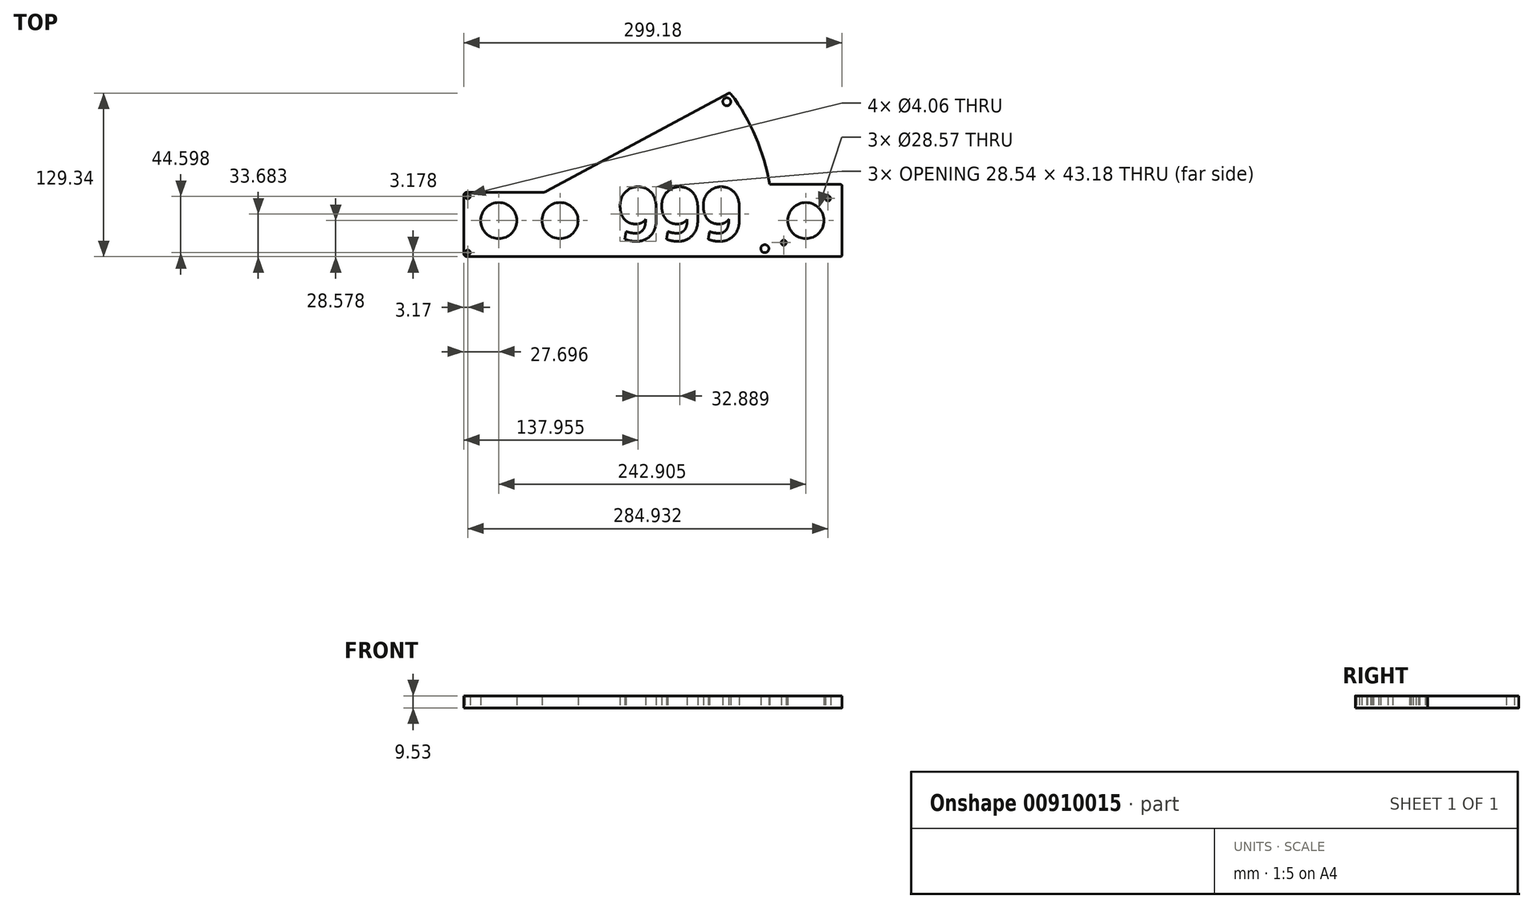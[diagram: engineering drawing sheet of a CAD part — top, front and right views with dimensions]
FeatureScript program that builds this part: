
annotation { "Feature Type Name" : "Feature", "Feature Type Description" : "" }
export const myFeature = defineFeature(function(context is Context, id is Id, definition is map)
    precondition{}
    {
        {
            var Q0;
            Q0=qCreatedBy(makeId("Top.planeOp"),FACE);
            var sketch = newSketch(context, id + "F0", { "sketchPlane" : qUnion([Q0])});
            skCircle(sketch, "E0", {"center": v(-130.35, 17.45) * mm, "radius": 14.29 * mm});
            skCircle(sketch, "E1", {"center": v(-130.35, 17.45) * mm, "radius": 25.4 * mm});
            skLineSegment(sketch, "E2", {"start": v(-130.35, -11.13) * mm, "end": v(36.65, -11.13) * mm});
            skArc(sketch, "E3", {"start": v(35.48, 46.02) * mm, "mid": v(24.35, 83.66) * mm, "end": v(4.8, 117.7) * mm});
            skLineSegment(sketch, "E4", {"start": v(3.18, 118.06) * mm, "end": v(-140.97, 40.58) * mm});
            skPoint(sketch, "E5.visualSharp", {"position": v(37.92, -11.13) * mm});
            skArc(sketch, "E5.filletArc", {"start": v(36.65, -11.13) * mm, "mid": v(37.55, -10.76) * mm, "end": v(37.92, -9.86) * mm});
            skPoint(sketch, "E6.visualSharp", {"position": v(4.14, 118.57) * mm});
            skArc(sketch, "E6.filletArc", {"start": v(4.8, 117.7) * mm, "mid": v(4.06, 118.18) * mm, "end": v(3.18, 118.06) * mm});
            skCircle(sketch, "E7", {"center": v(1.53, 111.4) * mm, "radius": 3.17 * mm});
            skCircle(sketch, "E8", {"center": v(31.57, -4.78) * mm, "radius": 3.17 * mm});
            skArc(sketch, "E9", {"start": v(25.22, 17.45) * mm, "mid": v(16.9, 67.65) * mm, "end": v(-7.18, 112.49) * mm});
            skLineSegment(sketch, "E10", {"start": v(-155.75, -11.13) * mm, "end": v(-130.35, -11.13) * mm});
            skLineSegment(sketch, "E11", {"start": v(25.22, 17.45) * mm, "end": v(25.22, -11.13) * mm});
            skLineSegment(sketch, "E12", {"start": v(-155.75, -11.13) * mm, "end": v(-204.01, -11.13) * mm});
            skLineSegment(sketch, "E13", {"start": v(-206.55, -8.59) * mm, "end": v(-206.55, 37.28) * mm});
            skLineSegment(sketch, "E14", {"start": v(-204.01, 39.82) * mm, "end": v(-143.98, 39.82) * mm});
            skPoint(sketch, "E15.visualSharp", {"position": v(-206.55, 39.82) * mm});
            skArc(sketch, "E15.filletArc", {"start": v(-204.01, 39.82) * mm, "mid": v(-205.81, 39.08) * mm, "end": v(-206.55, 37.28) * mm});
            skPoint(sketch, "E16.visualSharp", {"position": v(-142.38, 39.82) * mm});
            skArc(sketch, "E16.filletArc", {"start": v(-143.98, 39.82) * mm, "mid": v(-142.43, 40.01) * mm, "end": v(-140.97, 40.58) * mm});
            skPoint(sketch, "E17.visualSharp", {"position": v(-206.55, -11.13) * mm});
            skArc(sketch, "E17.filletArc", {"start": v(-206.55, -8.59) * mm, "mid": v(-205.81, -10.38) * mm, "end": v(-204.01, -11.13) * mm});
            skPoint(sketch, "E18.start.orphan", {"position": v(-155.75, 17.45) * mm});
            skCircle(sketch, "E19", {"center": v(-178.85, 17.45) * mm, "radius": 14.29 * mm});
            skLineSegment(sketch, "E20", {"start": v(36.65, -11.13) * mm, "end": v(91.36, -11.13) * mm});
            skLineSegment(sketch, "E21", {"start": v(92.63, -9.86) * mm, "end": v(92.63, 44.75) * mm});
            skLineSegment(sketch, "E22", {"start": v(91.36, 46.02) * mm, "end": v(35.48, 46.02) * mm});
            skCircle(sketch, "E23", {"center": v(81.55, 34.95) * mm, "radius": 2.03 * mm});
            skCircle(sketch, "E24", {"center": v(46.55, -0.05) * mm, "radius": 2.03 * mm});
            skCircle(sketch, "E25", {"center": v(64.05, 17.45) * mm, "radius": 14.29 * mm});
            skCircle(sketch, "E26", {"center": v(-203.38, 36.65) * mm, "radius": 2.03 * mm});
            skCircle(sketch, "E27", {"center": v(-203.38, -7.95) * mm, "radius": 2.03 * mm});
            skText(sketch, "E28", { "text": "999", "fontName": "RobotoSlab-Bold.ttf"});
            skPoint(sketch, "E29.visualSharp", {"position": v(92.63, 46.02) * mm});
            skArc(sketch, "E29.filletArc", {"start": v(92.63, 44.75) * mm, "mid": v(92.25, 45.65) * mm, "end": v(91.36, 46.02) * mm});
            skPoint(sketch, "E30.visualSharp", {"position": v(92.63, -11.13) * mm});
            skArc(sketch, "E30.filletArc", {"start": v(91.36, -11.13) * mm, "mid": v(92.25, -10.76) * mm, "end": v(92.63, -9.86) * mm});
            const initialGuessF0  = {"E28": [-0.08468, 0.00157, 1, 0, 0.0425]};
            skSetInitialGuess(sketch, initialGuessF0);
            skSolve(sketch);
        }
        {
            var Q0;
            Q0=makeQuery(id+"F0.imprint","IMPRINT",FACE,{"disambiguationData":[TD([[makeQuery(id+"F0.imprint","IMPRINT",EDGE,{"derivedFrom":sQuery(id+"F0.wireOp",EDGE,"E3")}),1.0]])]});
            var Q1;
            Q1=makeQuery(id+"F0.imprint","IMPRINT",FACE,{"disambiguationData":[TD([[makeQuery(id+"F0.imprint","IMPRINT",EDGE,{"derivedFrom":sQuery(id+"F0.wireOp",EDGE,"E1")}),-1.0]])]});
            var Q2;
            Q2=makeQuery(id+"F0.imprint","IMPRINT",FACE,{"disambiguationData":[TD([[makeQuery(id+"F0.imprint","IMPRINT",EDGE,{"derivedFrom":sQuery(id+"F0.wireOp",EDGE,"E0")}),-1.0]])]});
            extrude(context, id + "F1", {"entities" : qUnion([Q0, Q1, Q2]), "depth" : 9.52 * mm, "offsetDistance" : 25.4 * mm});
        }
    });
